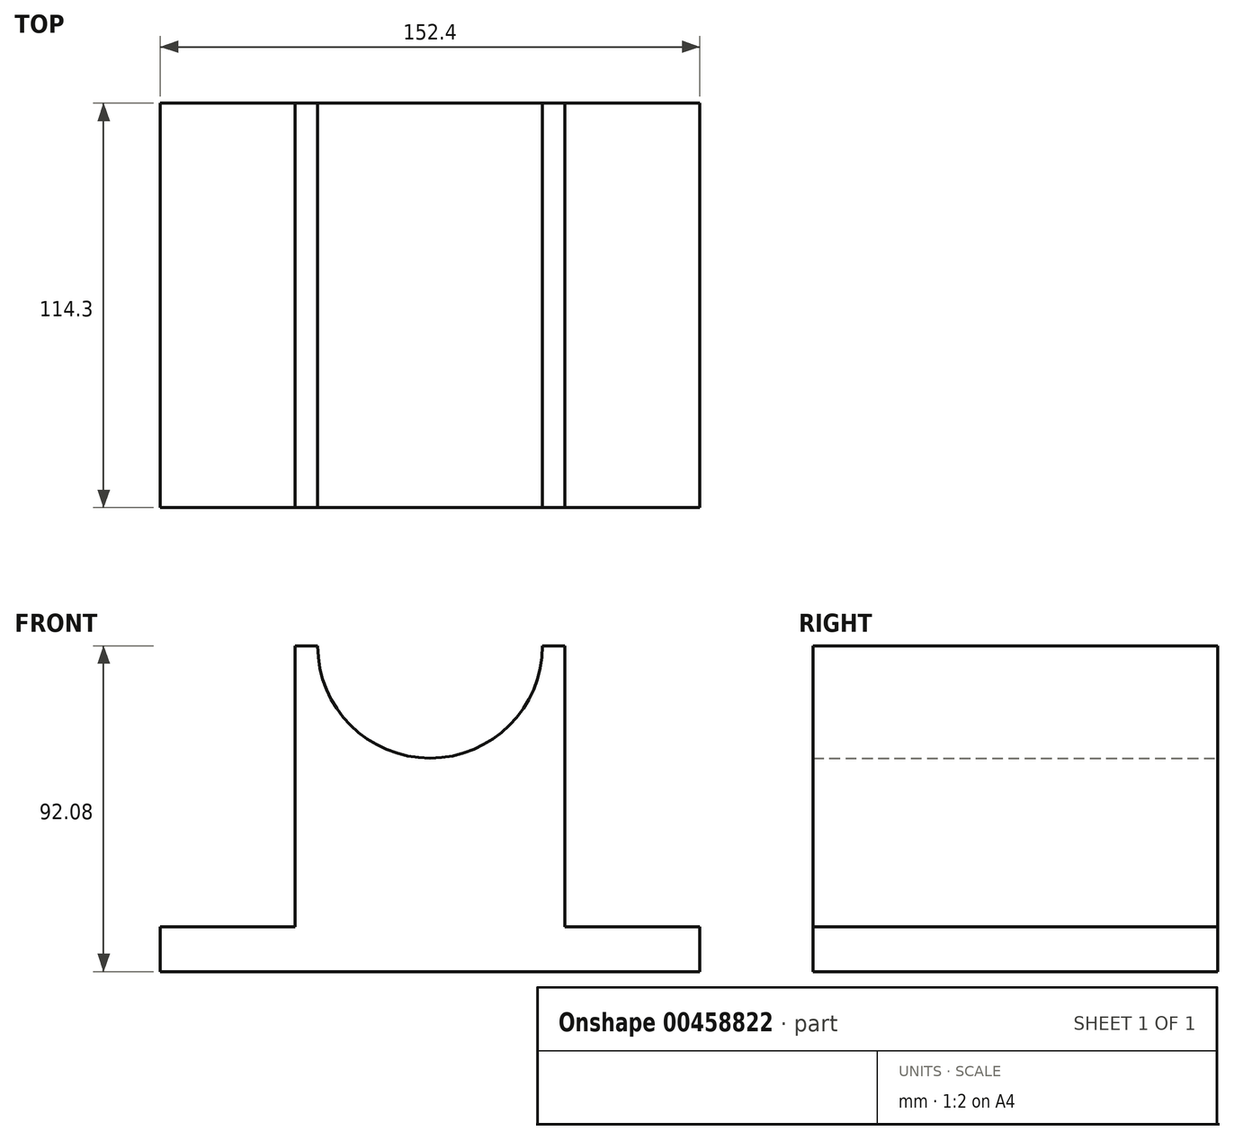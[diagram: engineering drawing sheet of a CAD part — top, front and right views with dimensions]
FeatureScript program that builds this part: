
annotation { "Feature Type Name" : "Feature", "Feature Type Description" : "" }
export const myFeature = defineFeature(function(context is Context, id is Id, definition is map)
    precondition{}
    {
        {
            var Q0;
            Q0=qCreatedBy(makeId("Front.planeOp"),FACE);
            var sketch = newSketch(context, id + "F0", { "sketchPlane" : qUnion([Q0])});
            skLineSegment(sketch, "E0.top", {"start": v(-42.08, 0) * mm, "end": v(34.12, 0) * mm});
            skLineSegment(sketch, "E0.left", {"start": v(-42.08, 92.08) * mm, "end": v(-42.08, 0) * mm});
            skLineSegment(sketch, "E0.right", {"start": v(34.12, 92.08) * mm, "end": v(34.12, 0) * mm});
            skLineSegment(sketch, "E1.bottom", {"start": v(72.22, 12.7) * mm, "end": v(-80.18, 12.7) * mm});
            skLineSegment(sketch, "E1.left", {"start": v(72.22, 12.7) * mm, "end": v(72.22, 0) * mm});
            skLineSegment(sketch, "E1.right", {"start": v(-80.18, 12.7) * mm, "end": v(-80.18, 0) * mm});
            skLineSegment(sketch, "E2", {"start": v(-80.18, 0) * mm, "end": v(72.22, 0) * mm});
            skArc(sketch, "E3", {"start": v(-35.73, 92.08) * mm, "mid": v(-3.98, 60.33) * mm, "end": v(27.77, 92.08) * mm});
            skLineSegment(sketch, "E4", {"start": v(-35.73, 92.08) * mm, "end": v(-42.08, 92.08) * mm});
            skLineSegment(sketch, "E5", {"start": v(27.77, 92.08) * mm, "end": v(34.12, 92.08) * mm});
            skSolve(sketch);
        }
        {
            var Q0;
            Q0=qSketchRegion(id+"F0",true);
            extrude(context, id + "F1", {"entities" : qUnion([Q0]), "depth" : 114.3 * mm});
        }
    });
